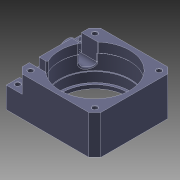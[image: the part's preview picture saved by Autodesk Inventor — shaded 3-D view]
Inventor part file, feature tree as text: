
AUTODESK INVENTOR PART (.ipt)
format: ipt  version: 2022 (Build 260153000, 153)  size: 420,352 bytes
history: native  units: mm
features: other x14, sketch x11, extrude x9, projected_geometry x5, fillet x3, chamfer x3, hole x2, mirror x2, revolve x2, reference x2
ambient origin geometry x8: Origin, YZ Plane, XZ Plane, XY Plane, X Axis, Y Axis, Z Axis, Center Point
bodies: Body1 (feature_tree), Body2 (feature_tree)
feature tree (53):
  other  "Твердое тело1"
  other  "РабПлоскость1"
  sketch  "Эскиз1"
  other  "РабПлоскость2"
  other  "РабПлоскость3"
  other  "РабПлоскость4"
  extrude  "Выдавливание1"  Depth=3.4mm
  extrude  "Выдавливание2"  Depth=40.0mm TaperAngle=360.0deg
  extrude  "Выдавливание3"  Depth=10.0mm TaperAngle=0.0deg
  extrude  "Выдавливание4"  Depth=0.7mm
  extrude  "Выдавливание5"  Depth=28.0mm TaperAngle=0.0deg
  fillet  "Сопряжение1"  Radius=58.0mm
  hole  "Отверстие1"  [1 undecoded]
  other  "РабПлоскость5"
  mirror  "Зеркальное отражение1"
  sketch  "Эскиз7"
  revolve  "Вращение1"
  revolve  "Вращение2"
  extrude  "Выдавливание6"  Depth=8.0mm
  fillet  "Сопряжение2"  Radius=15.0mm
  fillet  "Сопряжение3"  Radius=8.0mm
  other  "РабПлоскость6"
  extrude  "Выдавливание8"  Depth=0.5mm
  extrude  "Выдавливание9"  TaperAngle=45.0deg  [1 undecoded]
  mirror  "Зеркальное отражение2"
  chamfer  "Фаска1"  Distance=12.5mm
  extrude  "Выдавливание10"  Depth=0.1mm
  chamfer  "Фаска2"  Angle=90.0deg  [1 undecoded]
  chamfer  "Фаска3"  Distance=8.0mm
  hole  "Отверстие2"  [1 undecoded]
  reference  "Ссылка1"
  sketch  "Эскиз2"
  reference  "Ссылка2"
  sketch  "Эскиз3"
  sketch  "Эскиз4"
  projected_geometry  "Спроецированная петля1"
  sketch  "Эскиз6"
  projected_geometry  "Спроецированная петля2"
  sketch  "Эскиз8"
  projected_geometry  "Спроецированная петля3"
  sketch  "Эскиз11"
  sketch  "Эскиз12"
  projected_geometry  "Спроецированная петля8"
  projected_geometry  "Спроецированная петля9"
  sketch  "Эскиз13"
  other  "Твердое тело2"
  sketch  "Эскиз14"
  parser-record x2  (decoder bookkeeping rows leaked as tree rows — omitted from the tree; the rows remain in map.json)
  other  "Nema17.iam"
  other  "Насос Основание_нижнее:1"
  other  "Полумуфта:1"
  other  "Основание_нижнее:1"
note: 4 required parameter values undecoded (feature->parameter linkage not recoverable at this tier; creation-order binding heuristic only, values carry confidence <= 0.55)
note: 2 file-system paths scrubbed to <path> (originals preserved in map.json)
